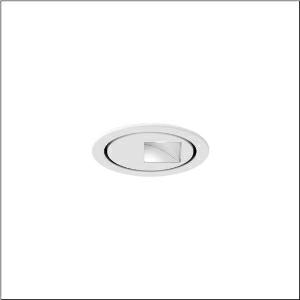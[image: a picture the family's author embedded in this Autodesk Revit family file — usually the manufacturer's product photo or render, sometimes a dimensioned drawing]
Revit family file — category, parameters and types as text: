
# Revit family: lunis_11_micro_round_51dj11cd1wf21
name_source: partatom
category: Lighting Fixtures
units: mm (PartAtom-declared; Revit-internal decimal feet)

## family parameters
Cut with Voids When Loaded = No
Host = Face
Light Source = No
Part Type = Normal
Room Calculation Point = No
Round Connector Dimension = Use Diameter
Shared = No

## types (1)
- Lunis 11 micro round (1 x LED 3000K / CRI = 80 (unbekannt), 1320 lm, 3000K)
    Apparent Load = 20 VA
    CIE Flux Codes = 42 75 96 100 100
    Color Rendering = 80
    Color Temperature = 3000K
    Default Elevation = 1800 mm
    Description = Lunis 11 micro round, downlight, light control with wallwasher, of highly reflective aluminium, highly specular, light emission: direct distribution, LED rated luminous flux: 1.320lm, light colour: 830, with terminal, 5-pole, mains connection: 220..230V, AC, 50/60Hz, LED module, of aluminium, highly specular, white, diameter: 114mm, clamping range: 1..40mm, recessing ring, of plastic, traffic white (RAL 9016), protection rating (complete): IP20, insulation class (complete): insulation class II (safety insulation), certification: CE, permissible ambient temperature for indoor applications: 0..+35°C, packaging unit: 1 piece
    Height = 0 mm  [stored 0 ft]
    Lamp = 1 x LED 3000K / CRI >= 80 (unbekannt)
    Lamp Light Flux = 1320 lm
    Lamp count = 1
    Length = 114 mm
    Luminous efficacy = 67 lm/W
    Manufacturer = Siteco
    ModVariant = No
    Model = 51DJ11CD1WF21
    Mounting Place = Ceiling
    Mounting Type = Recessed
    Number of Poles = 1
    OnlyDefault = Yes
    Power Factor = 1
    Product Name = Lunis 11 micro round
    Product group = downlight
    ProductGroupID = 400
    Protection Class = Protection class II
    Protection Degree = IP 20
    RLX_Detail_Level = 1
    RLX_Emergency_Light_Flux = 0 lm
    RLX_Emergency_Type = 0
    RLX_Emergency_Type_DB = No
    RlxData = <blob elided: 40409 chars, md5=ed6661b4>
    Socket = socket
    Standby Power = 0 W
    System Light Flux = 1320 lm
    System Power = 20 W
    Type Comments = Product without accessories
    Type Image = l_1004773.jpg
    URL = http://relux.com
    VarID = ---
    Voltage = 0 V
    Weight = 0.00 kg
    Width = 114 mm

note: [stored X ft] marks values corroborated as IEEE doubles in the binary element streams (Revit-internal decimal feet)

## geometry (parser evidence)
native form markers: Blend x4, Sweep x12
no freeform markers — native parametric forms only
